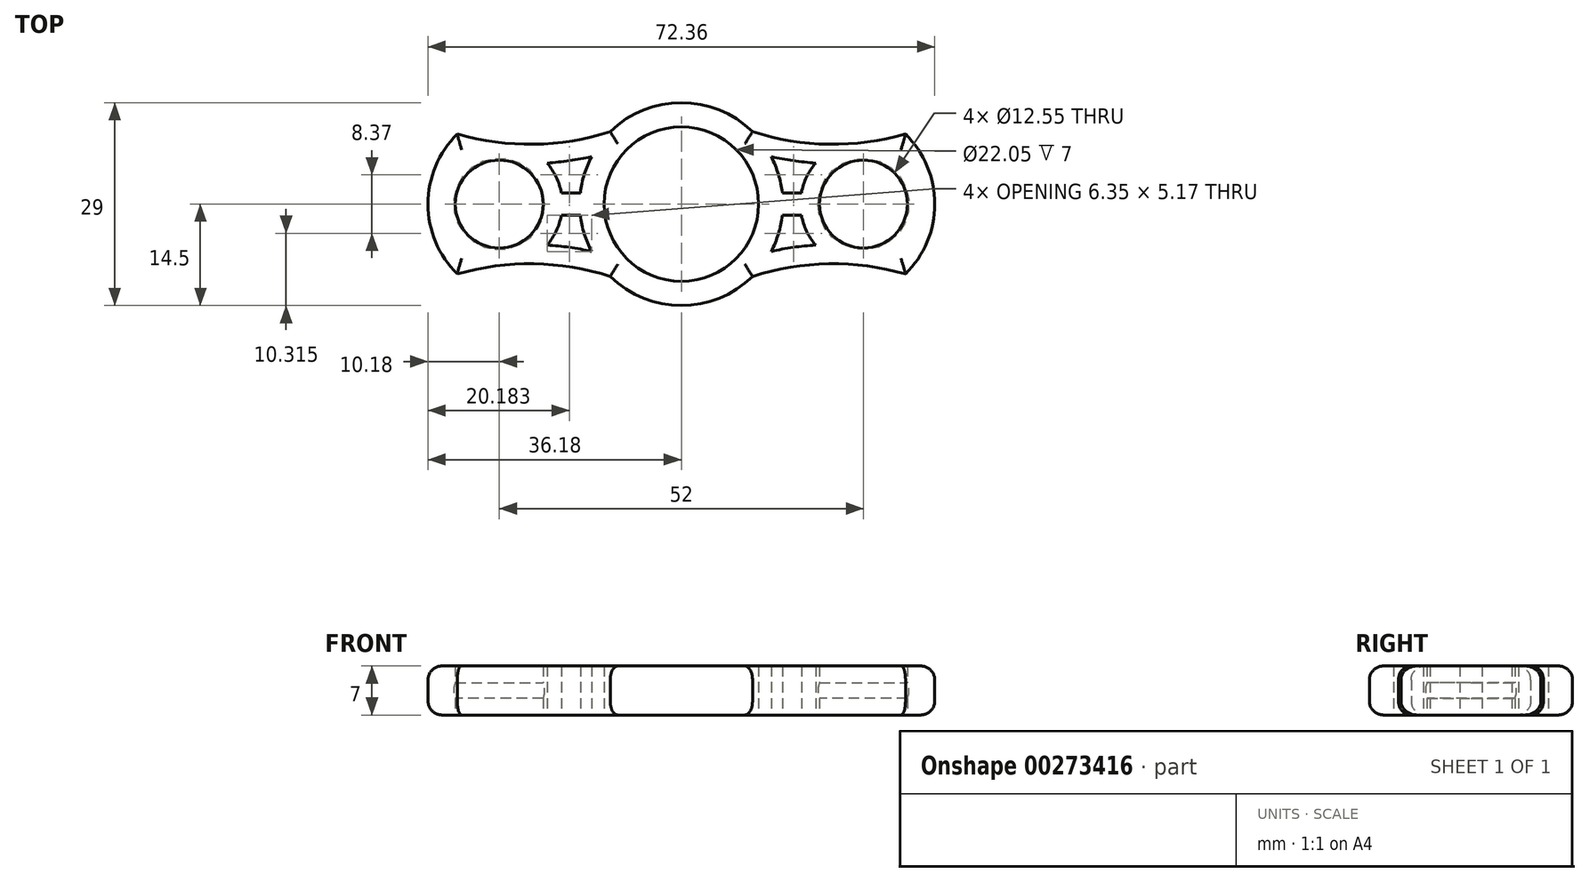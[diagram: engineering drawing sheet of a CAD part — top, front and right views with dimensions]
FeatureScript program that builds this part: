
annotation { "Feature Type Name" : "Feature", "Feature Type Description" : "" }
export const myFeature = defineFeature(function(context is Context, id is Id, definition is map)
    precondition{}
    {
        {
            var Q0;
            Q0=qCreatedBy(makeId("Top.planeOp"),FACE);
            var sketch = newSketch(context, id + "F0", { "sketchPlane" : qUnion([Q0])});
            skCircle(sketch, "E0", {"center": v(0, 0) * mm, "radius": 11.02 * mm});
            skLineSegment(sketch, "E1", {"start": v(26, 0) * mm, "end": v(0, 0) * mm, "construction": true});
            skArc(sketch, "E2", {"start": v(-10.16, -10.35) * mm, "mid": v(0, -14.5) * mm, "end": v(10.16, -10.35) * mm});
            skCircle(sketch, "E3", {"center": v(26, 0) * mm, "radius": 6.28 * mm});
            skLineSegment(sketch, "E4.MirrorCS", {"start": v(-26, 0) * mm, "end": v(0, 0) * mm, "construction": true});
            skCircle(sketch, "E5.MirrorC", {"center": v(-26, 0) * mm, "radius": 6.28 * mm});
            skArc(sketch, "E6", {"start": v(-10.16, -10.35) * mm, "mid": v(-21.05, -8.54) * mm, "end": v(-32, -10) * mm});
            skArc(sketch, "E7.MirrorCS", {"start": v(-10.16, 10.35) * mm, "mid": v(-21.05, 8.54) * mm, "end": v(-32, 10) * mm});
            skLineSegment(sketch, "E8", {"start": v(-32, 10) * mm, "end": v(-32, -10) * mm, "construction": true});
            skArc(sketch, "E9", {"start": v(-32, 10) * mm, "mid": v(-36.18, 0) * mm, "end": v(-32, -10) * mm});
            skArc(sketch, "E10.MirrorCS", {"start": v(10.16, 10.35) * mm, "mid": v(21.05, 8.54) * mm, "end": v(32, 10) * mm});
            skArc(sketch, "E11.MirrorCS", {"start": v(10.16, -10.35) * mm, "mid": v(21.05, -8.54) * mm, "end": v(32, -10) * mm});
            skArc(sketch, "E12.MirrorCS", {"start": v(32, 10) * mm, "mid": v(36.18, 0) * mm, "end": v(32, -10) * mm});
            skArc(sketch, "E13.trimOffspring", {"start": v(10.16, 10.35) * mm, "mid": v(0, 14.5) * mm, "end": v(-10.16, 10.35) * mm});
            skArc(sketch, "E14", {"start": v(-19.17, -5.86) * mm, "mid": v(-17.87, -3.87) * mm, "end": v(-17.14, -1.6) * mm});
            skArc(sketch, "E15", {"start": v(-12.82, 6.77) * mm, "mid": v(-13.86, 4.26) * mm, "end": v(-14.41, 1.6) * mm});
            skLineSegment(sketch, "E16", {"start": v(-17.14, 1.6) * mm, "end": v(-14.41, 1.6) * mm});
            skLineSegment(sketch, "E17.MirrorCS", {"start": v(-17.14, -1.6) * mm, "end": v(-14.41, -1.6) * mm});
            skArc(sketch, "E18.0", {"start": v(-12.82, 6.77) * mm, "mid": v(-15.98, 6.19) * mm, "end": v(-19.17, 5.86) * mm});
            skArc(sketch, "E19.trimOffspring", {"start": v(-31.6, 7.04) * mm, "mid": v(-32.18, 7.2) * mm, "end": v(-32.76, 7.36) * mm});
            skArc(sketch, "E20.trimOffspring", {"start": v(-31.6, 7.04) * mm, "mid": v(-31.8, 6.88) * mm, "end": v(-32, 6.7) * mm});
            skArc(sketch, "E21.MirrorCS", {"start": v(-12.82, -6.77) * mm, "mid": v(-15.98, -6.19) * mm, "end": v(-19.17, -5.86) * mm});
            skArc(sketch, "E22.trimOffspring", {"start": v(-17.14, 1.6) * mm, "mid": v(-17.87, 3.87) * mm, "end": v(-19.17, 5.86) * mm});
            skArc(sketch, "E23.trimOffspring", {"start": v(-14.41, -1.6) * mm, "mid": v(-13.86, -4.26) * mm, "end": v(-12.82, -6.77) * mm});
            skArc(sketch, "E24.MirrorCS", {"start": v(12.82, 6.77) * mm, "mid": v(15.98, 6.19) * mm, "end": v(19.17, 5.86) * mm});
            skArc(sketch, "E25.MirrorCS", {"start": v(17.14, 1.6) * mm, "mid": v(17.87, 3.87) * mm, "end": v(19.17, 5.86) * mm});
            skLineSegment(sketch, "E26.MirrorCS", {"start": v(17.14, 1.6) * mm, "end": v(14.41, 1.6) * mm});
            skArc(sketch, "E27.MirrorCS", {"start": v(12.82, 6.77) * mm, "mid": v(13.86, 4.26) * mm, "end": v(14.41, 1.6) * mm});
            skLineSegment(sketch, "E28.MirrorCS", {"start": v(17.14, -1.6) * mm, "end": v(14.41, -1.6) * mm});
            skArc(sketch, "E29.MirrorCS", {"start": v(19.17, -5.86) * mm, "mid": v(17.87, -3.87) * mm, "end": v(17.14, -1.6) * mm});
            skArc(sketch, "E30.MirrorCS", {"start": v(14.41, -1.6) * mm, "mid": v(13.86, -4.26) * mm, "end": v(12.82, -6.77) * mm});
            skArc(sketch, "E31.MirrorCS", {"start": v(12.82, -6.77) * mm, "mid": v(15.98, -6.19) * mm, "end": v(19.17, -5.86) * mm});
            skSolve(sketch);
        }
        {
            var Q0;
            Q0=makeQuery(id+"F0.imprint","IMPRINT",FACE,{"disambiguationData":[TD([[makeQuery(id+"F0.imprint","IMPRINT",EDGE,{"derivedFrom":sQuery(id+"F0.wireOp",EDGE,"E0")}),-1.0]])]});
            extrude(context, id + "F1", {"entities" : qUnion([Q0]), "depth" : 7 * mm});
        }
        {
            var Q0;
            Q0=makeQuery(id+"F1.opExtrude","CAP_EDGE",EDGE,{"disambiguationData":[OSD([sQuery(id+"F0.wireOp",EDGE,"E9")])],"isStart":false});
            var Q1;
            Q1=makeQuery(id+"F1.opExtrude","CAP_EDGE",EDGE,{"disambiguationData":[OSD([sQuery(id+"F0.wireOp",EDGE,"E2")])],"isStart":false});
            var Q2;
            Q2=makeQuery(id+"F1.opExtrude","CAP_EDGE",EDGE,{"disambiguationData":[OSD([sQuery(id+"F0.wireOp",EDGE,"E13.trimOffspring")])],"isStart":false});
            var Q3;
            Q3=makeQuery(id+"F1.opExtrude","CAP_EDGE",EDGE,{"disambiguationData":[OSD([sQuery(id+"F0.wireOp",EDGE,"E12.MirrorCS")])],"isStart":false});
            var Q4;
            Q4=makeQuery(id+"F1.opExtrude","CAP_EDGE",EDGE,{"disambiguationData":[OSD([sQuery(id+"F0.wireOp",EDGE,"E7.MirrorCS")])],"isStart":false});
            var Q5;
            Q5=makeQuery(id+"F1.opExtrude","CAP_EDGE",EDGE,{"disambiguationData":[OSD([sQuery(id+"F0.wireOp",EDGE,"E6")])],"isStart":false});
            var Q6;
            Q6=makeQuery(id+"F1.opExtrude","CAP_EDGE",EDGE,{"disambiguationData":[OSD([sQuery(id+"F0.wireOp",EDGE,"E11.MirrorCS")])],"isStart":false});
            var Q7;
            Q7=makeQuery(id+"F1.opExtrude","CAP_EDGE",EDGE,{"disambiguationData":[OSD([sQuery(id+"F0.wireOp",EDGE,"E10.MirrorCS")])],"isStart":false});
            var Q8;
            Q8=makeQuery(id+"F1.opExtrude","CAP_EDGE",EDGE,{"disambiguationData":[OSD([sQuery(id+"F0.wireOp",EDGE,"E7.MirrorCS")])],"isStart":true});
            var Q9;
            Q9=makeQuery(id+"F1.opExtrude","CAP_EDGE",EDGE,{"disambiguationData":[OSD([sQuery(id+"F0.wireOp",EDGE,"E9")])],"isStart":true});
            var Q10;
            Q10=makeQuery(id+"F1.opExtrude","CAP_EDGE",EDGE,{"disambiguationData":[OSD([sQuery(id+"F0.wireOp",EDGE,"E2")])],"isStart":true});
            var Q11;
            Q11=makeQuery(id+"F1.opExtrude","CAP_EDGE",EDGE,{"disambiguationData":[OSD([sQuery(id+"F0.wireOp",EDGE,"E13.trimOffspring")])],"isStart":true});
            var Q12;
            Q12=makeQuery(id+"F1.opExtrude","CAP_EDGE",EDGE,{"disambiguationData":[OSD([sQuery(id+"F0.wireOp",EDGE,"E10.MirrorCS")])],"isStart":true});
            var Q13;
            Q13=makeQuery(id+"F1.opExtrude","CAP_EDGE",EDGE,{"disambiguationData":[OSD([sQuery(id+"F0.wireOp",EDGE,"E12.MirrorCS")])],"isStart":true});
            var Q14;
            Q14=makeQuery(id+"F1.opExtrude","CAP_EDGE",EDGE,{"disambiguationData":[OSD([sQuery(id+"F0.wireOp",EDGE,"E11.MirrorCS")])],"isStart":true});
            var Q15;
            Q15=makeQuery(id+"F1.opExtrude","CAP_EDGE",EDGE,{"disambiguationData":[OSD([sQuery(id+"F0.wireOp",EDGE,"E6")])],"isStart":true});
            fillet(context, id + "F2", {"entities" : qUnion([Q0, Q1, Q2, Q3, Q4, Q5, Q6, Q7, Q8, Q9, Q10, Q11, Q12, Q13, Q14, Q15]), "radius" : 2 * mm, "tangentPropagation" : true, "allowEdgeOverflow" : false});
        }
        {
            var Q0;
            Q0=qCreatedBy(makeId("Front.planeOp"),FACE);
            var sketch = newSketch(context, id + "F3", { "sketchPlane" : qUnion([Q0])});
            skLineSegment(sketch, "E32", {"start": v(0, 0) * mm, "end": v(0, 3.5) * mm, "construction": true});
            skLineSegment(sketch, "E33", {"start": v(0, 0) * mm, "end": v(19.7, 0) * mm, "construction": true});
            skLineSegment(sketch, "E34", {"start": v(26, 7) * mm, "end": v(26, 0) * mm});
            skCircle(sketch, "E35", {"center": v(26, 3.5) * mm, "radius": 6.35 * mm, "construction": true});
            skCircle(sketch, "E36", {"center": v(22.3, 3.5) * mm, "radius": 2.8 * mm});
            skLineSegment(sketch, "E37", {"start": v(26, 3.5) * mm, "end": v(0, 3.5) * mm, "construction": true});
            skCircle(sketch, "E38", {"center": v(31.1, 3.5) * mm, "radius": 1.54 * mm});
            skLineSegment(sketch, "E39", {"start": v(19.75, 8.4) * mm, "end": v(19.75, -3.31) * mm, "construction": true});
            skLineSegment(sketch, "E40.MirrorCS", {"start": v(32.25, 8.4) * mm, "end": v(32.25, -3.31) * mm, "construction": true});
            skSolve(sketch);
        }
        {
            var Q0;
            Q0=makeQuery(id+"F3.imprint","IMPRINT",FACE,{"disambiguationData":[TD([[makeQuery(id+"F3.imprint","IMPRINT",EDGE,{"derivedFrom":sQuery(id+"F3.wireOp",EDGE,"E36")}),1.0]])]});
            var Q1;
            Q1=sQuery(id+"F3.wireOp",EDGE,"plMtQdIa-XCyh-ZVgV-Gdkr-hLrOiwfthBWz");
            var Q2;
            Q2=sQuery(id+"F3.wireOp",EDGE,"E34");
            revolve(context, id + "F4", {"operationType" : NewBodyOperationType.REMOVE, "entities" : qUnion([Q0]), "surfaceEntities" : qUnion([Q1]), "axis" : qUnion([Q2]), "revolveType" : RevolveType.FULL, "oppositeDirection" : true});
        }
        {
            var Q0;
            Q0=qCreatedBy(makeId("Front.planeOp"),FACE);
            var sketch = newSketch(context, id + "F5", { "sketchPlane" : qUnion([Q0])});
            skLineSegment(sketch, "E41", {"start": v(0, 0) * mm, "end": v(0, 3.5) * mm, "construction": true});
            skLineSegment(sketch, "E42", {"start": v(0, 3.5) * mm, "end": v(-26, 3.5) * mm, "construction": true});
            skCircle(sketch, "E43", {"center": v(-26, 3.5) * mm, "radius": 6.35 * mm, "construction": true});
            skLineSegment(sketch, "E44", {"start": v(-26, 7.8) * mm, "end": v(-26, -2.18) * mm});
            skCircle(sketch, "E45", {"center": v(-22.3, 3.5) * mm, "radius": 2.8 * mm});
            skSolve(sketch);
        }
        {
            var Q0;
            Q0=makeQuery(id+"F5.imprint","IMPRINT",FACE,{"disambiguationData":[TD([[makeQuery(id+"F5.imprint","IMPRINT",EDGE,{"derivedFrom":sQuery(id+"F5.wireOp",EDGE,"E45")}),1.0]])]});
            var Q1;
            Q1=sQuery(id+"F5.wireOp",EDGE,"E44");
            revolve(context, id + "F6", {"operationType" : NewBodyOperationType.REMOVE, "entities" : qUnion([Q0]), "axis" : qUnion([Q1]), "revolveType" : RevolveType.FULL});
        }
    });
